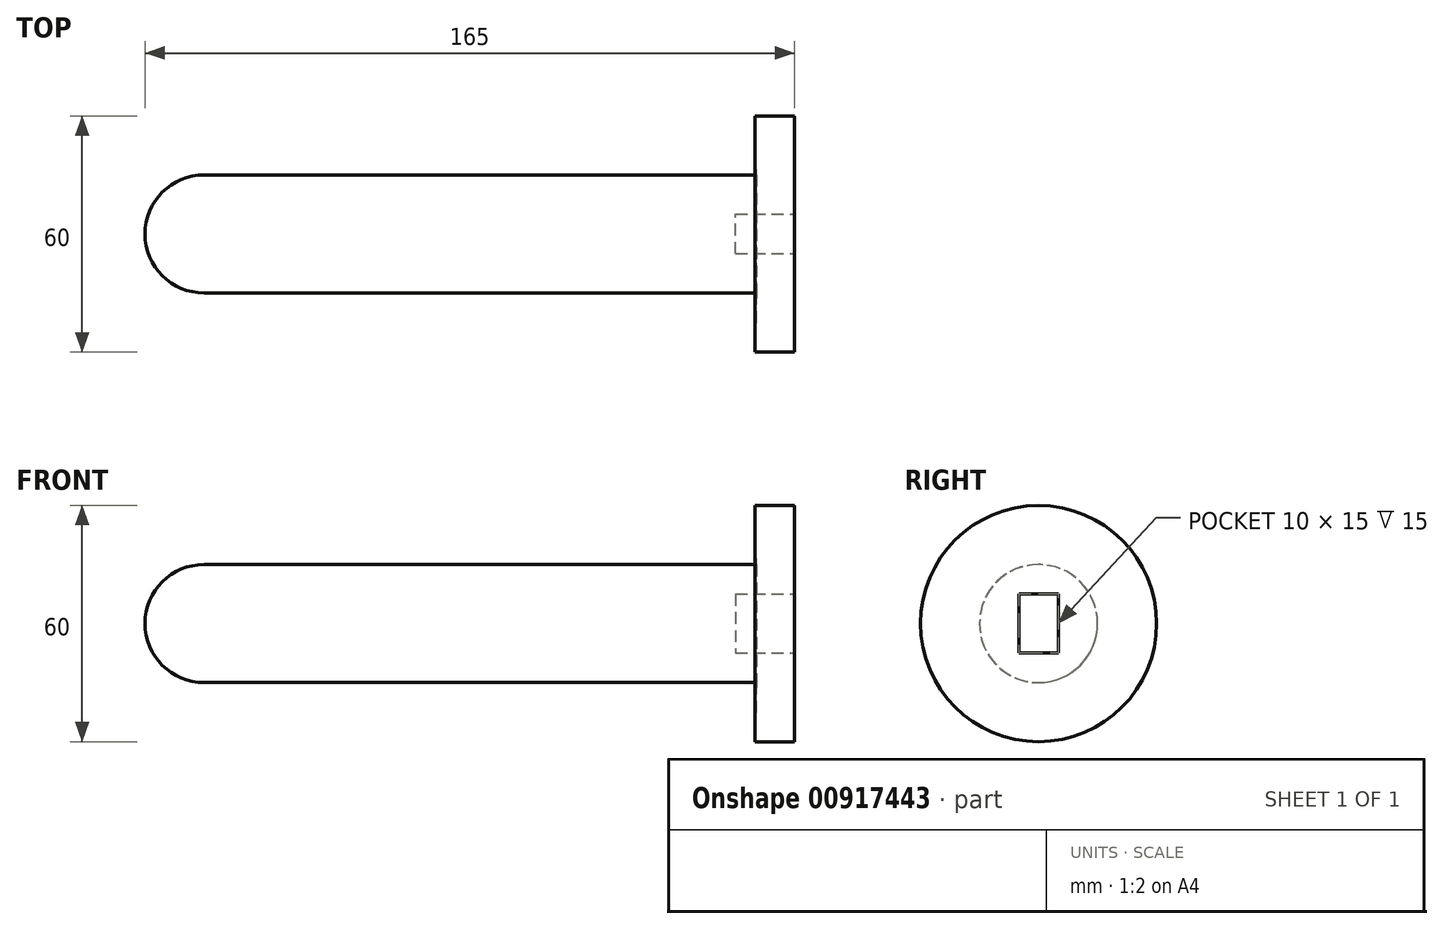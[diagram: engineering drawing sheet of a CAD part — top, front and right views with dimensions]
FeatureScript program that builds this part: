
annotation { "Feature Type Name" : "Feature", "Feature Type Description" : "" }
export const myFeature = defineFeature(function(context is Context, id is Id, definition is map)
    precondition{}
    {
        {
            var Q0;
            Q0=qCreatedBy(makeId("Front.planeOp"),FACE);
            var sketch = newSketch(context, id + "F0", { "sketchPlane" : qUnion([Q0])});
            skLineSegment(sketch, "E0", {"start": v(0, 0) * mm, "end": v(0, 30) * mm});
            skArc(sketch, "E1", {"start": v(0, 30) * mm, "mid": v(-15, 15) * mm, "end": v(0, 0) * mm});
            skSolve(sketch);
        }
        {
            var Q0;
            Q0=qCreatedBy(makeId("Front.planeOp"),FACE);
            var sketch = newSketch(context, id + "F1", { "sketchPlane" : qUnion([Q0])});
            skLineSegment(sketch, "E2.bottom", {"start": v(0, 15) * mm, "end": v(150, 15) * mm});
            skLineSegment(sketch, "E2.top", {"start": v(0, 0) * mm, "end": v(150, 0) * mm});
            skLineSegment(sketch, "E2.left", {"start": v(0, 15) * mm, "end": v(0, 0) * mm});
            skLineSegment(sketch, "E2.right", {"start": v(150, 15) * mm, "end": v(150, 0) * mm});
            skLineSegment(sketch, "E3.right", {"start": v(140.31, 0) * mm, "end": v(140.31, -0.33) * mm});
            skLineSegment(sketch, "E4.bottom", {"start": v(150, 15) * mm, "end": v(138.1, 15) * mm});
            skLineSegment(sketch, "E4.top", {"start": v(150, -15) * mm, "end": v(140, -15) * mm});
            skLineSegment(sketch, "E4.left", {"start": v(150, -15) * mm, "end": v(150, 15) * mm});
            skLineSegment(sketch, "E5", {"start": v(140.31, 0) * mm, "end": v(140, -15) * mm});
            skLineSegment(sketch, "E6.bottom", {"start": v(130.31, 0) * mm, "end": v(120.31, 0) * mm});
            skLineSegment(sketch, "E6.top", {"start": v(130.31, -15) * mm, "end": v(120.31, -15) * mm});
            skLineSegment(sketch, "E6.left", {"start": v(130.31, 0) * mm, "end": v(130.31, -15) * mm});
            skLineSegment(sketch, "E6.right", {"start": v(120.31, 0) * mm, "end": v(120.31, -15) * mm});
            skLineSegment(sketch, "E7.bottom", {"start": v(110.31, 0) * mm, "end": v(100.31, 0) * mm});
            skLineSegment(sketch, "E7.top", {"start": v(110.31, -15) * mm, "end": v(100.31, -15) * mm});
            skLineSegment(sketch, "E7.left", {"start": v(110.31, 0) * mm, "end": v(110.31, -15) * mm});
            skLineSegment(sketch, "E7.right", {"start": v(100.31, 0) * mm, "end": v(100.31, -15) * mm});
            skLineSegment(sketch, "E8.bottom", {"start": v(90.31, 0) * mm, "end": v(80.31, 0) * mm});
            skLineSegment(sketch, "E8.top", {"start": v(90.31, -15) * mm, "end": v(80.31, -15) * mm});
            skLineSegment(sketch, "E8.left", {"start": v(90.31, 0) * mm, "end": v(90.31, -15) * mm});
            skLineSegment(sketch, "E8.right", {"start": v(80.31, 0) * mm, "end": v(80.31, -15) * mm});
            skSolve(sketch);
        }
        {
            var Q0;
            {var subQ4=sQuery(id+"F1.wireOp",EDGE,"E4.top");Q0=makeQuery(id+"F1.imprint","IMPRINT",FACE,{"disambiguationData":[TD([[makeQuery(id+"F1.imprint","IMPRINT",EDGE,{"derivedFrom":subQ4}),-1.0]])]});}
            var Q1;
            Q1=makeQuery(id+"F1.imprint","IMPRINT",FACE,{"disambiguationData":[TD([[makeQuery(id+"F1.imprint","IMPRINT",EDGE,{"derivedFrom":sQuery(id+"F1.wireOp",EDGE,"E2.bottom")}),-1.0]])]});
            var Q2;
            Q2=makeQuery(id+"F1.imprint","IMPRINT",FACE,{"disambiguationData":[TD([[makeQuery(id+"F1.imprint","IMPRINT",EDGE,{"derivedFrom":sQuery(id+"F1.wireOp",EDGE,"E6.bottom")}),1.0]])]});
            var Q3;
            Q3=makeQuery(id+"F1.imprint","IMPRINT",FACE,{"disambiguationData":[TD([[makeQuery(id+"F1.imprint","IMPRINT",EDGE,{"derivedFrom":sQuery(id+"F1.wireOp",EDGE,"E7.bottom")}),1.0]])]});
            var Q4;
            Q4=makeQuery(id+"F1.imprint","IMPRINT",FACE,{"disambiguationData":[TD([[makeQuery(id+"F1.imprint","IMPRINT",EDGE,{"derivedFrom":sQuery(id+"F1.wireOp",EDGE,"E8.bottom")}),1.0]])]});
            var Q5;
            Q5=sQuery(id+"F1.wireOp",EDGE,"E2.bottom");
            revolve(context, id + "F2", {"surfaceOperationType" : NewSurfaceOperationType.NEW, "entities" : qUnion([Q0, Q1, Q2, Q3, Q4]), "axis" : qUnion([Q5]), "revolveType" : RevolveType.FULL});
        }
        {
            var Q0;
            Q0=makeQuery(id+"F2.opRevolve","SWEPT_FACE",FACE,{"disambiguationData":[OSD([sQuery(id+"F1.wireOp",EDGE,"E4.left")])]});
            var sketch = newSketch(context, id + "F3", { "sketchPlane" : qUnion([Q0])});
            skLineSegment(sketch, "E9.bottom", {"start": v(-5, 22.5) * mm, "end": v(5, 22.5) * mm});
            skLineSegment(sketch, "E9.top", {"start": v(-5, 7.5) * mm, "end": v(5, 7.5) * mm});
            skLineSegment(sketch, "E9.left", {"start": v(-5, 22.5) * mm, "end": v(-5, 7.5) * mm});
            skLineSegment(sketch, "E9.right", {"start": v(5, 22.5) * mm, "end": v(5, 7.5) * mm});
            skPoint(sketch, "E9.middle", {"position": v(0, 15) * mm});
            skSolve(sketch);
        }
        {
            var Q0;
            Q0=makeQuery(id+"F0.imprint","IMPRINT",FACE,{"disambiguationData":[TD([[makeQuery(id+"F0.imprint","IMPRINT",EDGE,{"derivedFrom":sQuery(id+"F0.wireOp",EDGE,"E0")}),1.0]])]});
            var Q1;
            Q1=sQuery(id+"F0.wireOp",EDGE,"E0");
            revolve(context, id + "F4", {"operationType" : NewBodyOperationType.ADD, "surfaceOperationType" : NewSurfaceOperationType.NEW, "entities" : qUnion([Q0]), "axis" : qUnion([Q1]), "revolveType" : RevolveType.FULL});
        }
        {
            var Q0;
            Q0=makeQuery(id+"F3.imprint","IMPRINT",FACE,{"disambiguationData":[TD([[makeQuery(id+"F3.imprint","IMPRINT",EDGE,{"derivedFrom":sQuery(id+"F3.wireOp",EDGE,"E9.bottom")}),-1.0]])]});
            extrude(context, id + "F5", {"entities" : qUnion([Q0]), "operationType" : NewBodyOperationType.REMOVE, "oppositeDirection" : true, "depth" : 15 * mm, "offsetDistance" : 25 * mm});
        }
    });
